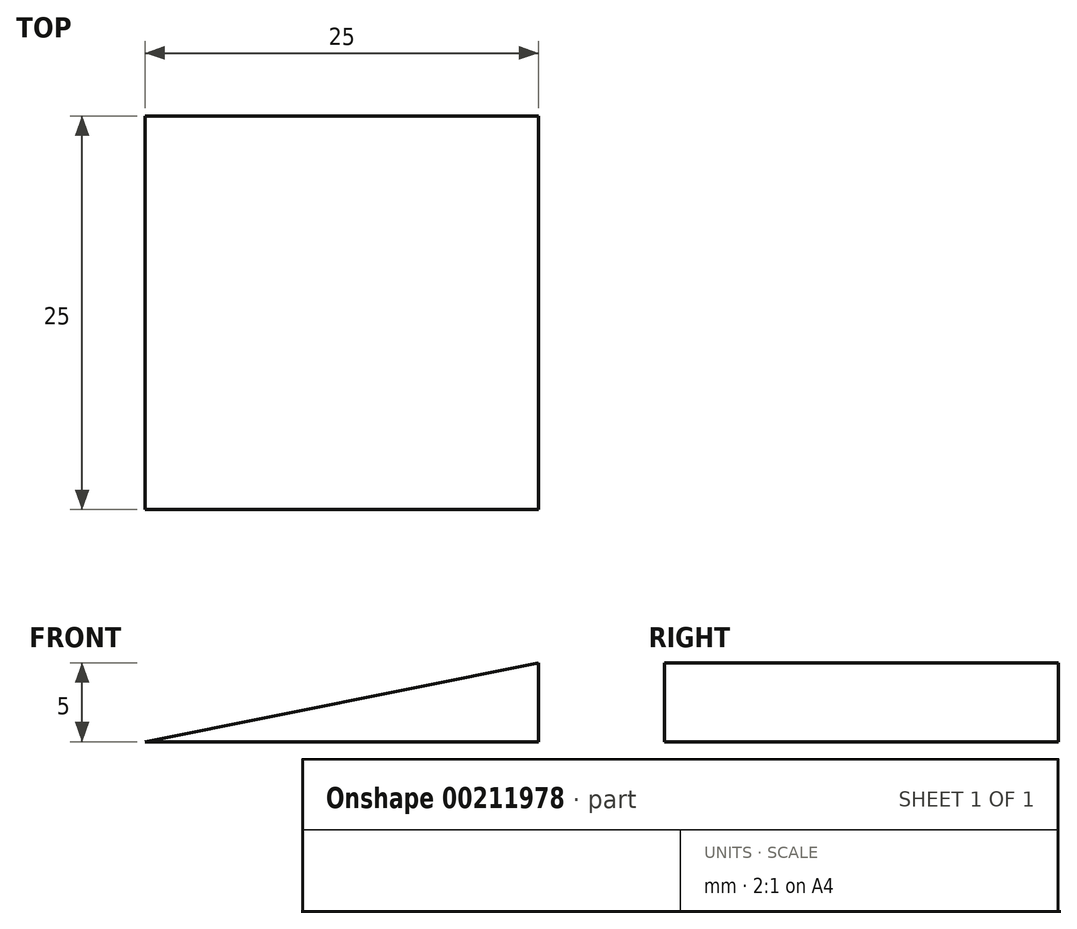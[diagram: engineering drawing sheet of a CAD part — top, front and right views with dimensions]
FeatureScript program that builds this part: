
annotation { "Feature Type Name" : "Feature", "Feature Type Description" : "" }
export const myFeature = defineFeature(function(context is Context, id is Id, definition is map)
    precondition{}
    {
        {
            var Q0;
            Q0=qCreatedBy(makeId("Front.planeOp"),FACE);
            var sketch = newSketch(context, id + "F0", { "sketchPlane" : qUnion([Q0])});
            skLineSegment(sketch, "E0", {"start": v(-12.57, 0) * mm, "end": v(12.43, 0) * mm});
            skLineSegment(sketch, "E1", {"start": v(12.43, 0) * mm, "end": v(12.43, 5) * mm});
            skLineSegment(sketch, "E2", {"start": v(12.43, 5) * mm, "end": v(-12.57, 0) * mm});
            skSolve(sketch);
        }
        {
            var Q0;
            Q0 = qSketchRegion(id + "F0", true);
            extrude(context, id + "F1", {"entities" : qUnion([Q0]), "depth" : 25 * mm});
        }
    });
